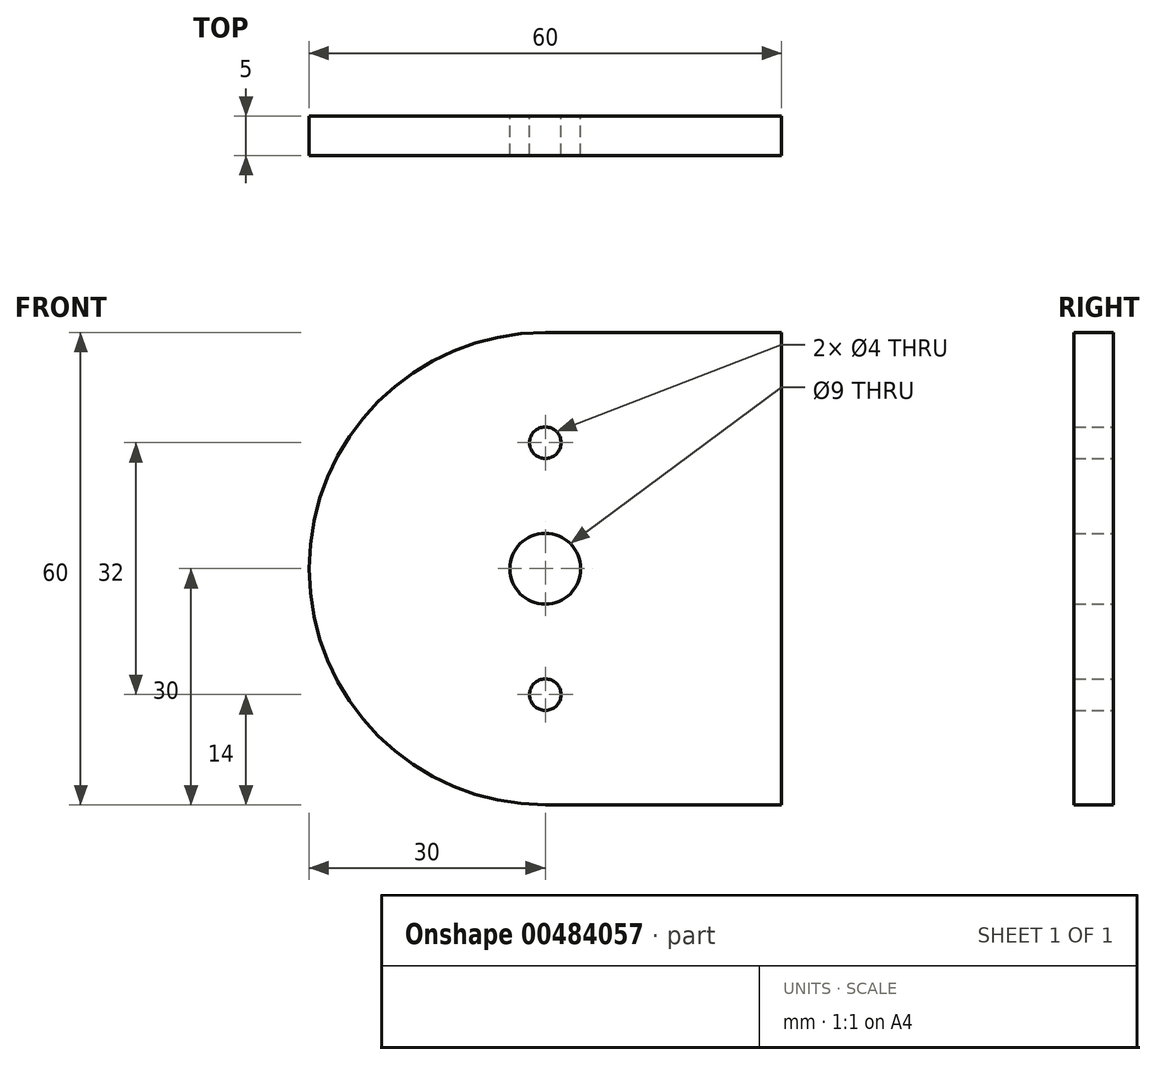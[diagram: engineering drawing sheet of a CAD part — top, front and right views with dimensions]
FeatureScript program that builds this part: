
annotation { "Feature Type Name" : "Feature", "Feature Type Description" : "" }
export const myFeature = defineFeature(function(context is Context, id is Id, definition is map)
    precondition{}
    {
        {
            var Q0;
            Q0=qCreatedBy(makeId("Front.planeOp"),FACE);
            var sketch = newSketch(context, id + "F0", { "sketchPlane" : qUnion([Q0])});
            skLineSegment(sketch, "E0.bottom", {"start": v(15, 30) * mm, "end": v(-15, 30) * mm});
            skLineSegment(sketch, "E0.top", {"start": v(15, -30) * mm, "end": v(-15, -30) * mm});
            skLineSegment(sketch, "E0.left", {"start": v(15, 30) * mm, "end": v(15, -30) * mm});
            skPoint(sketch, "E0.middle", {"position": v(0, 0) * mm});
            skArc(sketch, "E1", {"start": v(-15, 30) * mm, "mid": v(-45, 0) * mm, "end": v(-15, -30) * mm});
            skCircle(sketch, "E2", {"center": v(-15, 0) * mm, "radius": 4.5 * mm});
            skCircle(sketch, "E3", {"center": v(-15, 16) * mm, "radius": 2 * mm});
            skCircle(sketch, "E4", {"center": v(-15, -16) * mm, "radius": 2 * mm});
            skSolve(sketch);
        }
        {
            var Q0;
            Q0 = qSketchRegion(id + "F0", true);
            extrude(context, id + "F1", {"entities" : qUnion([Q0]), "depth" : 5 * mm});
        }
    });
